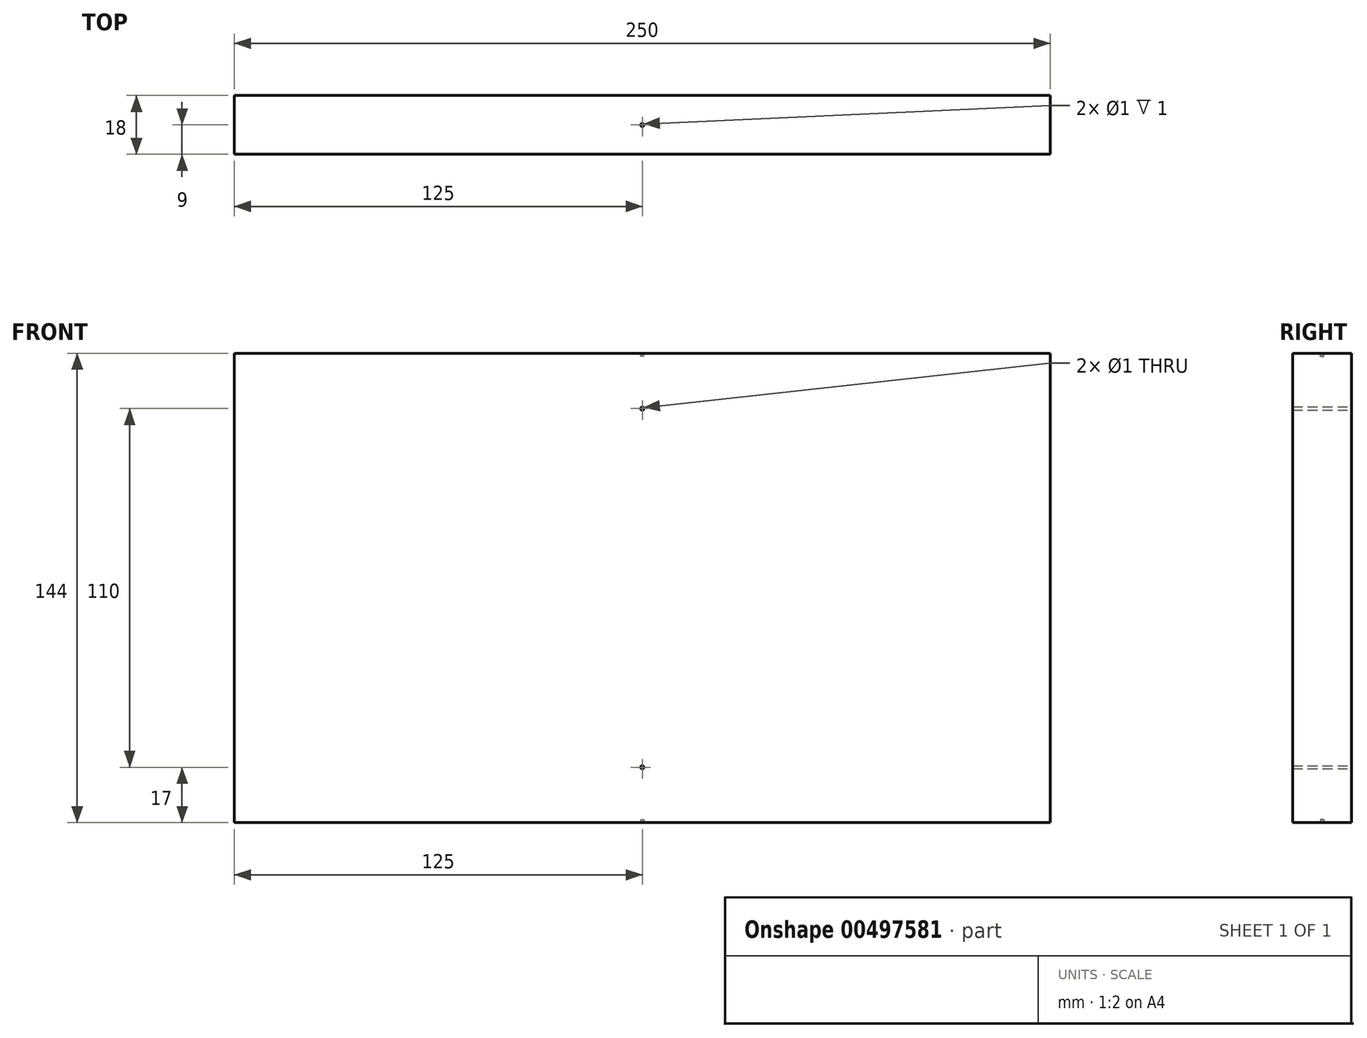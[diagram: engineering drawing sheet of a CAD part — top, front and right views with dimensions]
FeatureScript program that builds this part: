
annotation { "Feature Type Name" : "Feature", "Feature Type Description" : "" }
export const myFeature = defineFeature(function(context is Context, id is Id, definition is map)
    precondition{}
    {
        {
            var Q0;
            Q0=qCreatedBy(makeId("Front.planeOp"),FACE);
            var sketch = newSketch(context, id + "F0", { "sketchPlane" : qUnion([Q0])});
            skLineSegment(sketch, "E0.bottom", {"start": v(0, 0) * mm, "end": v(250, 0) * mm});
            skLineSegment(sketch, "E0.top", {"start": v(0, 144) * mm, "end": v(250, 144) * mm});
            skLineSegment(sketch, "E0.left", {"start": v(0, 0) * mm, "end": v(0, 144) * mm});
            skLineSegment(sketch, "E0.right", {"start": v(250, 0) * mm, "end": v(250, 144) * mm});
            skPoint(sketch, "E1.centerSnap0", {"position": v(125, 144) * mm});
            skLineSegment(sketch, "E2", {"start": v(0, 72) * mm, "end": v(250, 72) * mm, "construction": true});
            skCircle(sketch, "E3", {"center": v(125, 17) * mm, "radius": 0.5 * mm});
            skPoint(sketch, "E3.centerSnap0", {"position": v(125, 72) * mm});
            skCircle(sketch, "E4.MirrorC", {"center": v(125, 127) * mm, "radius": 0.5 * mm});
            skSolve(sketch);
        }
        {
            var Q0;
            Q0=qSketchRegion(id+"F0",true);
            extrude(context, id + "F1", {"entities" : qUnion([Q0]), "depth" : 18 * mm, "offsetDistance" : 25.4 * mm});
        }
        {
            var Q0;
            Q0=makeQuery(id+"F1.opExtrude","SWEPT_FACE",FACE,{"disambiguationData":[OSD([sQuery(id+"F0.wireOp",EDGE,"E0.bottom")])]});
            var sketch = newSketch(context, id + "F2", { "sketchPlane" : qUnion([Q0])});
            skCircle(sketch, "E5", {"center": v(125, 9) * mm, "radius": 0.5 * mm});
            skPoint(sketch, "E5.centerSnap0", {"position": v(125, 0) * mm});
            skPoint(sketch, "E5.centerSnap1", {"position": v(0, 9) * mm});
            skSolve(sketch);
        }
        {
            var Q0;
            Q0=qSketchRegion(id+"F2",true);
            extrude(context, id + "F3", {"entities" : qUnion([Q0]), "operationType" : NewBodyOperationType.REMOVE, "oppositeDirection" : true, "depth" : 1 * mm, "offsetDistance" : 25.4 * mm});
        }
        {
            var Q0;
            Q0=makeQuery(id+"F1.opExtrude","SWEPT_FACE",FACE,{"disambiguationData":[OSD([sQuery(id+"F0.wireOp",EDGE,"E0.top")])]});
            var sketch = newSketch(context, id + "F4", { "sketchPlane" : qUnion([Q0])});
            skCircle(sketch, "E6", {"center": v(125, -9) * mm, "radius": 0.5 * mm});
            skPoint(sketch, "E6.centerSnap0", {"position": v(125, -18) * mm});
            skPoint(sketch, "E6.centerSnap1", {"position": v(0, -9) * mm});
            skSolve(sketch);
        }
        {
            var Q0;
            Q0=qSketchRegion(id+"F4",true);
            extrude(context, id + "F5", {"entities" : qUnion([Q0]), "operationType" : NewBodyOperationType.REMOVE, "oppositeDirection" : true, "depth" : 1 * mm, "offsetDistance" : 25.4 * mm});
        }
    });
